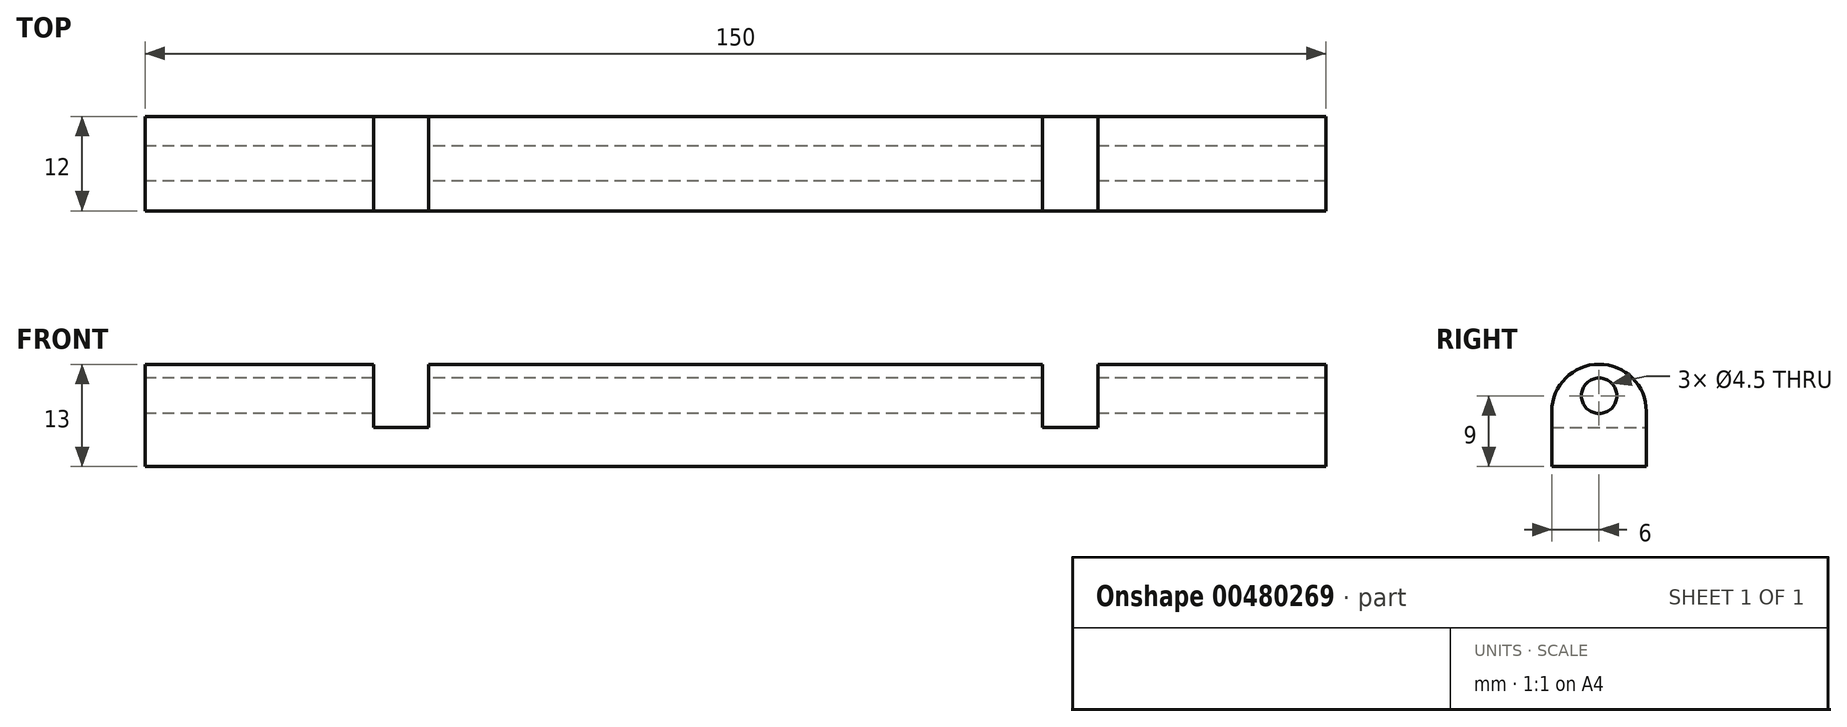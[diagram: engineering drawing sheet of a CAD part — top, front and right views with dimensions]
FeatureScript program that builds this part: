
annotation { "Feature Type Name" : "Feature", "Feature Type Description" : "" }
export const myFeature = defineFeature(function(context is Context, id is Id, definition is map)
    precondition{}
    {
        {
            var Q0;
            Q0=qCreatedBy(makeId("Top.planeOp"),FACE);
            var sketch = newSketch(context, id + "F0", { "sketchPlane" : qUnion([Q0])});
            skLineSegment(sketch, "E0.bottom", {"start": v(0, 0) * mm, "end": v(150, 0) * mm});
            skLineSegment(sketch, "E0.top", {"start": v(0, 12) * mm, "end": v(150, 12) * mm});
            skLineSegment(sketch, "E0.left", {"start": v(0, 0) * mm, "end": v(0, 12) * mm});
            skLineSegment(sketch, "E0.right", {"start": v(150, 0) * mm, "end": v(150, 12) * mm});
            skSolve(sketch);
        }
        {
            var Q0;
            Q0=makeQuery(id+"F0.imprint","IMPRINT",FACE,{"disambiguationData":[TD([[makeQuery(id+"F0.imprint","IMPRINT",EDGE,{"derivedFrom":sQuery(id+"F0.wireOp",EDGE,"E0.bottom")}),1.0]])]});
            extrude(context, id + "F1", {"entities" : qUnion([Q0]), "depth" : 3 * mm, "hasSecondDirection" : true, "secondDirectionOppositeDirection" : true, "secondDirectionDepth" : 2 * mm});
        }
        {
            var Q0;
            Q0=makeQuery(id+"F1.opExtrude","SWEPT_FACE",FACE,{"disambiguationData":[OSD([sQuery(id+"F0.wireOp",EDGE,"E0.left")])]});
            var sketch = newSketch(context, id + "F2", { "sketchPlane" : qUnion([Q0])});
            skLineSegment(sketch, "E1", {"start": v(-12, 3) * mm, "end": v(-12, 5) * mm});
            skLineSegment(sketch, "E2", {"start": v(0, 3) * mm, "end": v(0, 5) * mm});
            skArc(sketch, "E3", {"start": v(0, 5) * mm, "mid": v(-6, 11) * mm, "end": v(-12, 5) * mm});
            skCircle(sketch, "E4", {"center": v(-6, 7) * mm, "radius": 2.25 * mm});
            skSolve(sketch);
        }
        {
            var Q0;
            Q0=makeQuery(id+"F2.imprint","IMPRINT",FACE,{"disambiguationData":[TD([[makeQuery(id+"F2.imprint","IMPRINT",EDGE,{"derivedFrom":sQuery(id+"F2.wireOp",EDGE,"E1")}),-1.0]])]});
            extrude(context, id + "F3", {"entities" : qUnion([Q0]), "operationType" : NewBodyOperationType.ADD, "oppositeDirection" : true, "depth" : 29 * mm});
        }
        {
            var Q0;
            Q0=makeQuery(id+"F2.imprint","IMPRINT",FACE,{"disambiguationData":[TD([[makeQuery(id+"F2.imprint","IMPRINT",EDGE,{"derivedFrom":sQuery(id+"F2.wireOp",EDGE,"E1")}),-1.0]])]});
            extrude(context, id + "F4", {"entities" : qUnion([Q0]), "operationType" : NewBodyOperationType.ADD, "oppositeDirection" : true, "depth" : 114 * mm, "hasSecondDirection" : true, "secondDirectionOppositeDirection" : true, "secondDirectionDepth" : 36 * mm});
        }
        {
            var Q0;
            Q0=makeQuery(id+"F2.imprint","IMPRINT",FACE,{"disambiguationData":[TD([[makeQuery(id+"F2.imprint","IMPRINT",EDGE,{"derivedFrom":sQuery(id+"F2.wireOp",EDGE,"E1")}),-1.0]])]});
            extrude(context, id + "F5", {"entities" : qUnion([Q0]), "operationType" : NewBodyOperationType.ADD, "oppositeDirection" : true, "depth" : 150 * mm, "hasSecondDirection" : true, "secondDirectionOppositeDirection" : true, "secondDirectionDepth" : 121 * mm});
        }
    });
